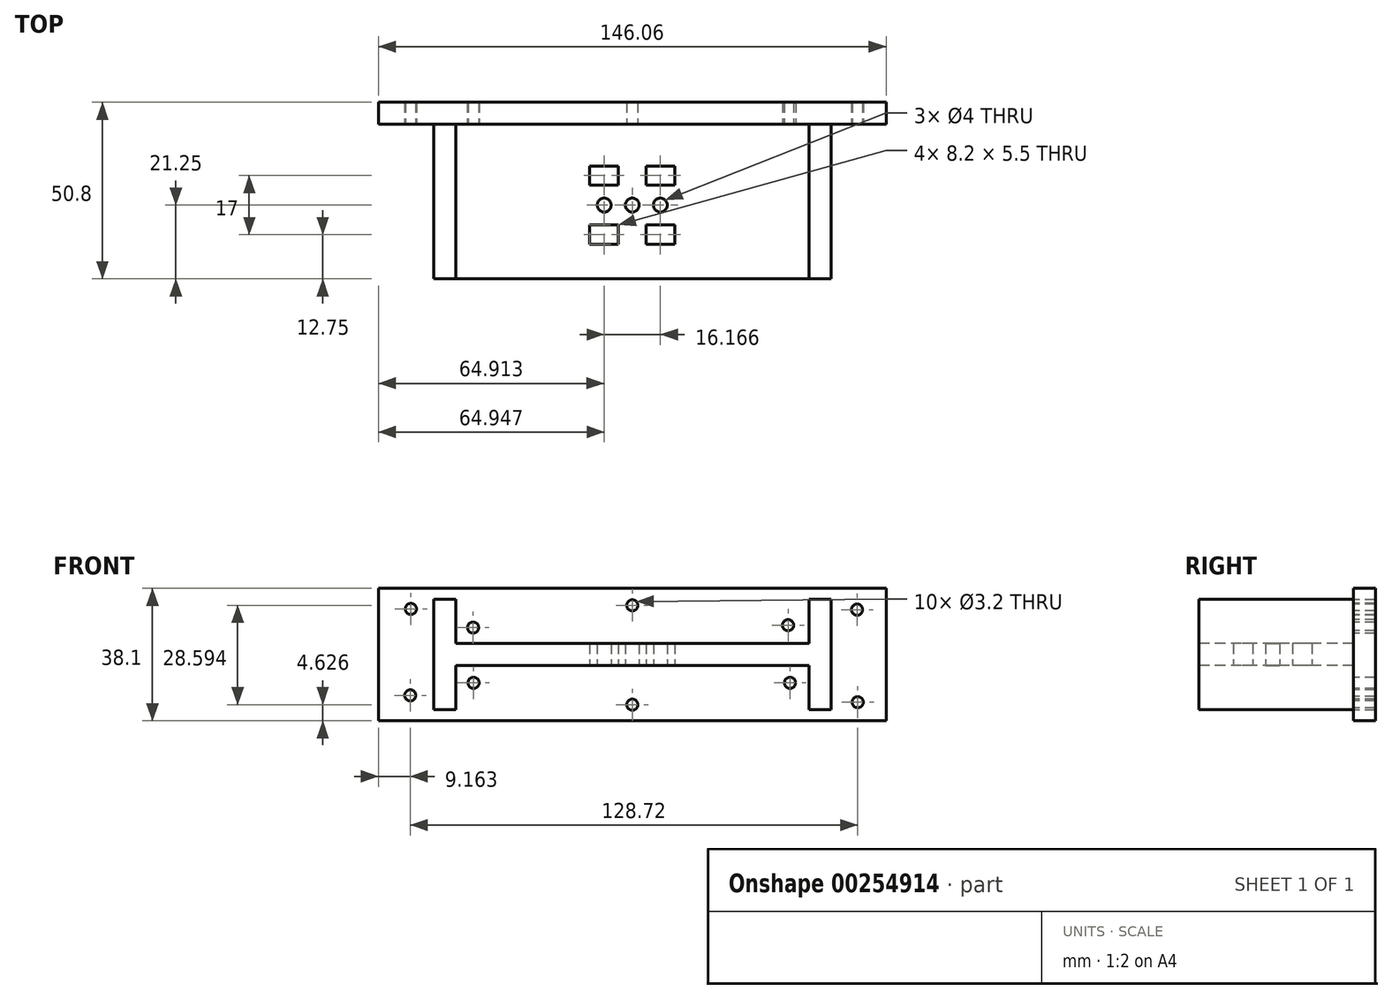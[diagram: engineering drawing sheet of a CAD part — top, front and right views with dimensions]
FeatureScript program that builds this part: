
annotation { "Feature Type Name" : "Feature", "Feature Type Description" : "" }
export const myFeature = defineFeature(function(context is Context, id is Id, definition is map)
    precondition{}
    {
        {
            var Q0;
            Q0=qCreatedBy(makeId("Front.planeOp"),FACE);
            var sketch = newSketch(context, id + "F0", { "sketchPlane" : qUnion([Q0])});
            skLineSegment(sketch, "E0.bottom", {"start": v(73.03, -19.05) * mm, "end": v(-73.03, -19.05) * mm});
            skLineSegment(sketch, "E0.top", {"start": v(73.03, 19.05) * mm, "end": v(-73.03, 19.05) * mm});
            skLineSegment(sketch, "E0.left", {"start": v(73.03, -19.05) * mm, "end": v(73.03, 19.05) * mm});
            skLineSegment(sketch, "E0.right", {"start": v(-73.03, -19.05) * mm, "end": v(-73.03, 19.05) * mm});
            skPoint(sketch, "E0.middle", {"position": v(0, 0) * mm});
            skSolve(sketch);
        }
        {
            var Q0;
            Q0 = qSketchRegion(id + "F0", true);
            extrude(context, id + "F1", {"entities" : qUnion([Q0]), "depth" : 6.35 * mm});
        }
        {
            var Q0;
            Q0=makeQuery(id+"F1.opExtrude","CAP_FACE",FACE,{"disambiguationData":[OSD([sQuery(id+"F0.wireOp",EDGE,"E0.bottom"),sQuery(id+"F0.wireOp",EDGE,"E0.top"),sQuery(id+"F0.wireOp",EDGE,"E0.left"),sQuery(id+"F0.wireOp",EDGE,"E0.right")])],"isStart":false});
            var sketch = newSketch(context, id + "F2", { "sketchPlane" : qUnion([Q0])});
            skLineSegment(sketch, "E1.bottom", {"start": v(50.8, -3.18) * mm, "end": v(-50.8, -3.18) * mm});
            skLineSegment(sketch, "E1.top", {"start": v(50.8, 3.18) * mm, "end": v(-50.8, 3.18) * mm});
            skLineSegment(sketch, "E1.left", {"start": v(50.8, -3.18) * mm, "end": v(50.8, 3.17) * mm});
            skLineSegment(sketch, "E1.right", {"start": v(-50.8, -3.18) * mm, "end": v(-50.8, 3.17) * mm});
            skPoint(sketch, "E1.middle", {"position": v(0, 0) * mm});
            skSolve(sketch);
        }
        {
            var Q0;
            Q0 = qSketchRegion(id + "F2", true);
            extrude(context, id + "F3", {"entities" : qUnion([Q0]), "operationType" : NewBodyOperationType.ADD, "depth" : 44.45 * mm});
        }
        {
            var Q0;
            Q0=makeQuery(id+"F1.opExtrude","CAP_FACE",FACE,{"disambiguationData":[OSD([sQuery(id+"F0.wireOp",EDGE,"E0.bottom"),sQuery(id+"F0.wireOp",EDGE,"E0.top"),sQuery(id+"F0.wireOp",EDGE,"E0.left"),sQuery(id+"F0.wireOp",EDGE,"E0.right")])],"isStart":false});
            var sketch = newSketch(context, id + "F4", { "sketchPlane" : qUnion([Q0])});
            skLineSegment(sketch, "E2.bottom", {"start": v(-50.78, 15.88) * mm, "end": v(-57.13, 15.88) * mm});
            skLineSegment(sketch, "E2.top", {"start": v(-50.78, -15.88) * mm, "end": v(-57.13, -15.88) * mm});
            skLineSegment(sketch, "E2.left", {"start": v(-50.78, 15.88) * mm, "end": v(-50.78, -15.88) * mm});
            skLineSegment(sketch, "E2.right", {"start": v(-57.13, 15.88) * mm, "end": v(-57.13, -15.88) * mm});
            skPoint(sketch, "E2.middle", {"position": v(-53.96, 0) * mm});
            skLineSegment(sketch, "E3.bottom", {"start": v(50.78, 15.88) * mm, "end": v(57.13, 15.88) * mm});
            skLineSegment(sketch, "E3.top", {"start": v(50.78, -15.88) * mm, "end": v(57.13, -15.88) * mm});
            skLineSegment(sketch, "E3.left", {"start": v(50.78, 15.88) * mm, "end": v(50.78, -15.88) * mm});
            skLineSegment(sketch, "E3.right", {"start": v(57.13, 15.88) * mm, "end": v(57.13, -15.88) * mm});
            skPoint(sketch, "E3.middle", {"position": v(53.96, 0) * mm});
            skSolve(sketch);
        }
        {
            var Q0;
            Q0 = qSketchRegion(id + "F4", true);
            extrude(context, id + "F5", {"entities" : qUnion([Q0]), "operationType" : NewBodyOperationType.ADD, "depth" : 44.45 * mm});
        }
        {
            var Q0;
            Q0=makeQuery(id+"F1.opExtrude","CAP_FACE",FACE,{"disambiguationData":[OSD([sQuery(id+"F0.wireOp",EDGE,"E0.bottom"),sQuery(id+"F0.wireOp",EDGE,"E0.top"),sQuery(id+"F0.wireOp",EDGE,"E0.left"),sQuery(id+"F0.wireOp",EDGE,"E0.right")])],"isStart":false});
            var sketch = newSketch(context, id + "F6", { "sketchPlane" : qUnion([Q0])});
            skCircle(sketch, "E4", {"center": v(0, 14.17) * mm, "radius": 1.6 * mm});
            skCircle(sketch, "E5", {"center": v(44.81, 8.45) * mm, "radius": 1.6 * mm});
            skCircle(sketch, "E6", {"center": v(64.66, 12.91) * mm, "radius": 1.6 * mm});
            skCircle(sketch, "E7", {"center": v(64.85, -13.7) * mm, "radius": 1.6 * mm});
            skCircle(sketch, "E8", {"center": v(45.37, -8.14) * mm, "radius": 1.6 * mm});
            skCircle(sketch, "E9", {"center": v(0, -14.42) * mm, "radius": 1.6 * mm});
            skCircle(sketch, "E10", {"center": v(-45.65, -8.14) * mm, "radius": 1.6 * mm});
            skCircle(sketch, "E11", {"center": v(-45.79, 7.75) * mm, "radius": 1.6 * mm});
            skCircle(sketch, "E12", {"center": v(-63.67, 13.1) * mm, "radius": 1.6 * mm});
            skCircle(sketch, "E13", {"center": v(-63.87, -11.73) * mm, "radius": 1.6 * mm});
            skSolve(sketch);
        }
        {
            var Q0;
            Q0 = qSketchRegion(id + "F6", true);
            extrude(context, id + "F7", {"entities" : qUnion([Q0]), "operationType" : NewBodyOperationType.REMOVE, "endBound" : BoundingType.THROUGH_ALL, "oppositeDirection" : true, "depth" : 25 * mm});
        }
        {
            var Q0;
            Q0=makeQuery(id+"F3.opExtrude","SWEPT_FACE",FACE,{"disambiguationData":[OSD([sQuery(id+"F2.wireOp",EDGE,"E1.bottom")])]});
            var sketch = newSketch(context, id + "F8", { "sketchPlane" : qUnion([Q0])});
            skLineSegment(sketch, "E14.bottom", {"start": v(-4.02, 35.3) * mm, "end": v(-12.22, 35.3) * mm});
            skLineSegment(sketch, "E14.top", {"start": v(-4.02, 40.8) * mm, "end": v(-12.22, 40.8) * mm});
            skLineSegment(sketch, "E14.left", {"start": v(-4.02, 35.3) * mm, "end": v(-4.02, 40.8) * mm});
            skLineSegment(sketch, "E14.right", {"start": v(-12.22, 35.3) * mm, "end": v(-12.22, 40.8) * mm});
            skPoint(sketch, "E14.middle", {"position": v(-8.12, 38.05) * mm});
            skLineSegment(sketch, "E15.bottom", {"start": v(12.18, 35.3) * mm, "end": v(3.98, 35.3) * mm});
            skLineSegment(sketch, "E15.top", {"start": v(12.18, 40.8) * mm, "end": v(3.98, 40.8) * mm});
            skLineSegment(sketch, "E15.left", {"start": v(12.18, 35.3) * mm, "end": v(12.18, 40.8) * mm});
            skLineSegment(sketch, "E15.right", {"start": v(3.98, 35.3) * mm, "end": v(3.98, 40.8) * mm});
            skPoint(sketch, "E15.middle", {"position": v(8.08, 38.05) * mm});
            skLineSegment(sketch, "E16.bottom", {"start": v(-4.02, 18.3) * mm, "end": v(-12.22, 18.3) * mm});
            skLineSegment(sketch, "E16.top", {"start": v(-4.02, 23.8) * mm, "end": v(-12.22, 23.8) * mm});
            skLineSegment(sketch, "E16.left", {"start": v(-4.02, 18.3) * mm, "end": v(-4.02, 23.8) * mm});
            skLineSegment(sketch, "E16.right", {"start": v(-12.22, 18.3) * mm, "end": v(-12.22, 23.8) * mm});
            skPoint(sketch, "E16.middle", {"position": v(-8.12, 21.05) * mm});
            skLineSegment(sketch, "E17.bottom", {"start": v(12.18, 18.3) * mm, "end": v(3.98, 18.3) * mm});
            skLineSegment(sketch, "E17.top", {"start": v(12.18, 23.8) * mm, "end": v(3.98, 23.8) * mm});
            skLineSegment(sketch, "E17.left", {"start": v(12.18, 18.3) * mm, "end": v(12.18, 23.8) * mm});
            skLineSegment(sketch, "E17.right", {"start": v(3.98, 18.3) * mm, "end": v(3.98, 23.8) * mm});
            skPoint(sketch, "E17.middle", {"position": v(8.08, 21.05) * mm});
            skSolve(sketch);
        }
        {
            var Q0;
            Q0 = qSketchRegion(id + "F8", true);
            extrude(context, id + "F9", {"entities" : qUnion([Q0]), "operationType" : NewBodyOperationType.REMOVE, "endBound" : BoundingType.THROUGH_ALL, "oppositeDirection" : true, "depth" : 25 * mm});
        }
        {
            var Q0;
            Q0=makeQuery(id+"F3.opExtrude","SWEPT_FACE",FACE,{"disambiguationData":[OSD([sQuery(id+"F2.wireOp",EDGE,"E1.bottom")])]});
            var sketch = newSketch(context, id + "F10", { "sketchPlane" : qUnion([Q0])});
            skCircle(sketch, "E18", {"center": v(0, 29.55) * mm, "radius": 2 * mm});
            skCircle(sketch, "E19", {"center": v(8.08, 29.55) * mm, "radius": 2 * mm});
            skCircle(sketch, "E20", {"center": v(-8.08, 29.55) * mm, "radius": 2 * mm});
            skSolve(sketch);
        }
        {
            var Q0;
            Q0 = qSketchRegion(id + "F10", true);
            extrude(context, id + "F11", {"entities" : qUnion([Q0]), "operationType" : NewBodyOperationType.REMOVE, "endBound" : BoundingType.THROUGH_ALL, "oppositeDirection" : true, "depth" : 25 * mm});
        }
    });
